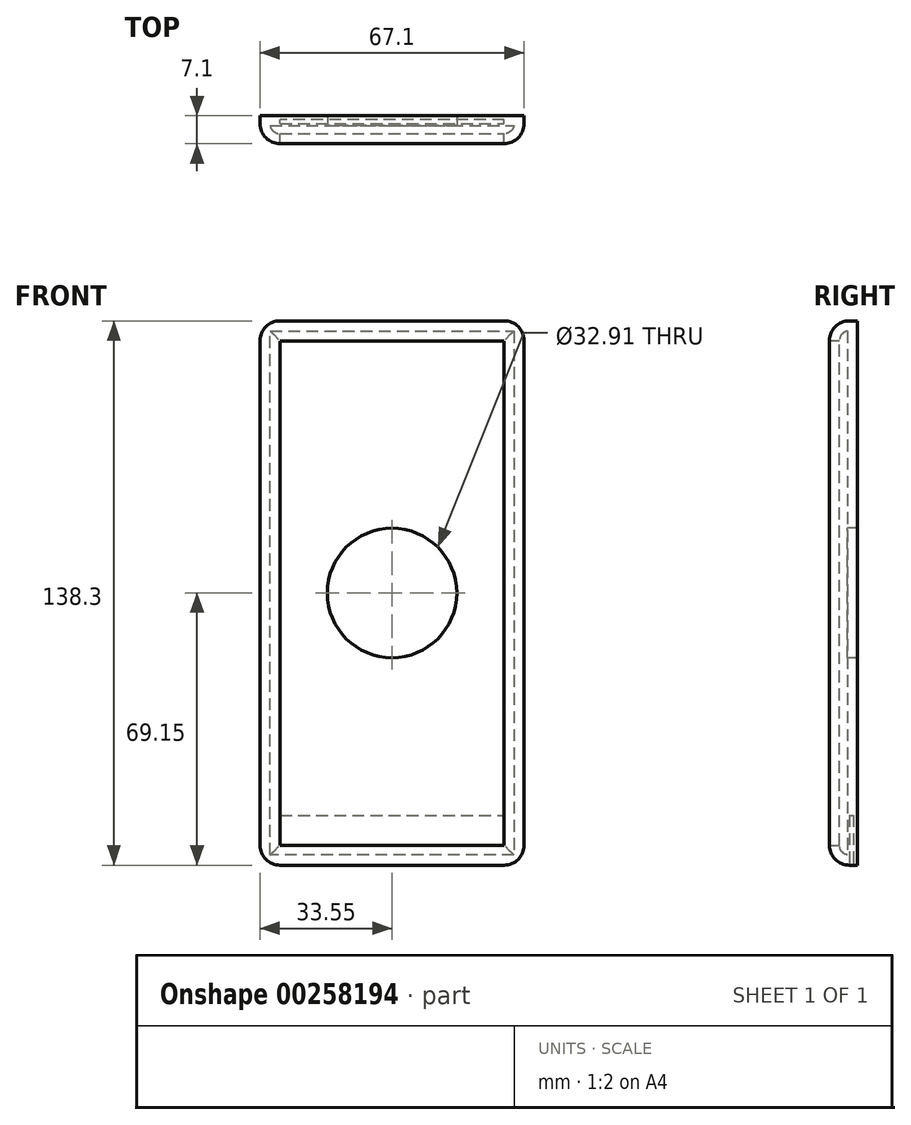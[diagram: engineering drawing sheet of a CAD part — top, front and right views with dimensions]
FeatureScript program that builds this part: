
annotation { "Feature Type Name" : "Feature", "Feature Type Description" : "" }
export const myFeature = defineFeature(function(context is Context, id is Id, definition is map)
    precondition{}
    {
        {
            var Q0;
            Q0=qCreatedBy(makeId("Front.planeOp"),FACE);
            var sketch = newSketch(context, id + "F0", { "sketchPlane" : qUnion([Q0])});
            skLineSegment(sketch, "E0.bottom", {"start": v(-33.55, 69.15) * mm, "end": v(33.55, 69.15) * mm});
            skLineSegment(sketch, "E0.top", {"start": v(-33.55, -69.15) * mm, "end": v(33.55, -69.15) * mm});
            skLineSegment(sketch, "E0.left", {"start": v(-33.55, 69.15) * mm, "end": v(-33.55, -69.15) * mm});
            skLineSegment(sketch, "E0.right", {"start": v(33.55, 69.15) * mm, "end": v(33.55, -69.15) * mm});
            skPoint(sketch, "E0.middle", {"position": v(0, 0) * mm});
            skSolve(sketch);
        }
        {
            var Q0;
            Q0=makeQuery(id+"F0.imprint","IMPRINT",FACE,{"disambiguationData":[TD([[makeQuery(id+"F0.imprint","IMPRINT",EDGE,{"derivedFrom":sQuery(id+"F0.wireOp",EDGE,"E0.bottom")}),-1.0]])]});
            extrude(context, id + "F1", {"entities" : qUnion([Q0]), "depth" : 7.1 * mm});
        }
        {
            var Q0;
            Q0=makeQuery(id+"F1.opExtrude","CAP_EDGE",EDGE,{"disambiguationData":[OSD([sQuery(id+"F0.wireOp",EDGE,"E0.bottom")])],"isStart":false});
            var Q1;
            Q1=makeQuery(id+"F1.opExtrude","CAP_EDGE",EDGE,{"disambiguationData":[OSD([sQuery(id+"F0.wireOp",EDGE,"E0.left")])],"isStart":false});
            var Q2;
            Q2=makeQuery(id+"F1.opExtrude","CAP_FACE",FACE,{"disambiguationData":[OSD([sQuery(id+"F0.wireOp",EDGE,"E0.bottom"),sQuery(id+"F0.wireOp",EDGE,"E0.top"),sQuery(id+"F0.wireOp",EDGE,"E0.left"),sQuery(id+"F0.wireOp",EDGE,"E0.right")])],"isStart":false});
            fillet(context, id + "F2", {"entities" : qUnion([Q0, Q1, Q2]), "radius" : 5.08 * mm, "tangentPropagation" : true, "allowEdgeOverflow" : false});
        }
        {
            var Q0;
            Q0=makeQuery(id+"F1.opExtrude","CAP_FACE",FACE,{"disambiguationData":[OSD([sQuery(id+"F0.wireOp",EDGE,"E0.bottom"),sQuery(id+"F0.wireOp",EDGE,"E0.top"),sQuery(id+"F0.wireOp",EDGE,"E0.left"),sQuery(id+"F0.wireOp",EDGE,"E0.right")])],"isStart":false});
            shell(context, id + "F3", {"entities" : qUnion([Q0]), "thickness" : 2.54 * mm});
        }
        {
            var Q0;
            Q0=makeQuery(id+"F2.opFillet","BLEND_EDGE",EDGE,{"blendedFrom":[makeQuery(id+"F1.opExtrude","CAP_EDGE",EDGE,{"disambiguationData":[OSD([sQuery(id+"F0.wireOp",EDGE,"E0.bottom")])],"isStart":false}),makeQuery(id+"F1.opExtrude","CAP_EDGE",EDGE,{"disambiguationData":[OSD([sQuery(id+"F0.wireOp",EDGE,"E0.left")])],"isStart":false})],"blendedInto":[]});
            var Q1;
            Q1=makeQuery(id+"F2.opFillet","BLEND_EDGE",EDGE,{"blendedFrom":[makeQuery(id+"F1.opExtrude","CAP_EDGE",EDGE,{"disambiguationData":[OSD([sQuery(id+"F0.wireOp",EDGE,"E0.bottom")])],"isStart":false}),makeQuery(id+"F1.opExtrude","CAP_EDGE",EDGE,{"disambiguationData":[OSD([sQuery(id+"F0.wireOp",EDGE,"E0.right")])],"isStart":false})],"blendedInto":[]});
            var Q2;
            Q2=makeQuery(id+"F2.opFillet","BLEND_EDGE",EDGE,{"blendedFrom":[makeQuery(id+"F1.opExtrude","CAP_EDGE",EDGE,{"disambiguationData":[OSD([sQuery(id+"F0.wireOp",EDGE,"E0.top")])],"isStart":false}),makeQuery(id+"F1.opExtrude","CAP_EDGE",EDGE,{"disambiguationData":[OSD([sQuery(id+"F0.wireOp",EDGE,"E0.right")])],"isStart":false})],"blendedInto":[]});
            var Q3;
            Q3=makeQuery(id+"F2.opFillet","BLEND_EDGE",EDGE,{"blendedFrom":[makeQuery(id+"F1.opExtrude","CAP_EDGE",EDGE,{"disambiguationData":[OSD([sQuery(id+"F0.wireOp",EDGE,"E0.top")])],"isStart":false}),makeQuery(id+"F1.opExtrude","CAP_EDGE",EDGE,{"disambiguationData":[OSD([sQuery(id+"F0.wireOp",EDGE,"E0.left")])],"isStart":false})],"blendedInto":[]});
            fillet(context, id + "F4", {"entities" : qUnion([Q0, Q1, Q2, Q3]), "radius" : 5.08 * mm, "tangentPropagation" : true, "allowEdgeOverflow" : false});
        }
        {
            var Q0;
            Q0=makeQuery(id+"F1.opExtrude","SWEPT_FACE",FACE,{"disambiguationData":[OSD([sQuery(id+"F0.wireOp",EDGE,"E0.top")])]});
            var sketch = newSketch(context, id + "F5", { "sketchPlane" : qUnion([Q0])});
            skPoint(sketch, "E1.oppositeSnap0", {"position": v(28.47, 1) * mm});
            skLineSegment(sketch, "E1.bottom", {"start": v(-29.15, 2.02) * mm, "end": v(29.44, 2.02) * mm});
            skLineSegment(sketch, "E1.top", {"start": v(-29.15, 1) * mm, "end": v(29.44, 1) * mm});
            skLineSegment(sketch, "E1.left", {"start": v(-29.15, 2.02) * mm, "end": v(-29.15, 1) * mm});
            skLineSegment(sketch, "E1.right", {"start": v(29.44, 2.02) * mm, "end": v(29.44, 1) * mm});
            skSolve(sketch);
        }
        {
            var Q0;
            Q0=makeQuery(id+"F5.imprint","IMPRINT",FACE,{"disambiguationData":[TD([[makeQuery(id+"F5.imprint","IMPRINT",EDGE,{"derivedFrom":sQuery(id+"F5.wireOp",EDGE,"E1.bottom")}),1.0]])]});
            extrude(context, id + "F6", {"entities" : qUnion([Q0]), "operationType" : NewBodyOperationType.REMOVE, "endBound" : BoundingType.SYMMETRIC, "oppositeDirection" : true, "depth" : 25.4 * mm});
        }
        {
            var Q0;
            Q0=makeQuery(id+"F3.opShell","OFFSET_FACE",FACE,{"disambiguationData":[OSD([sQuery(id+"F0.wireOp",EDGE,"E0.bottom"),sQuery(id+"F0.wireOp",EDGE,"E0.top"),sQuery(id+"F0.wireOp",EDGE,"E0.left"),sQuery(id+"F0.wireOp",EDGE,"E0.right")])]});
            var sketch = newSketch(context, id + "F7", { "sketchPlane" : qUnion([Q0])});
            skCircle(sketch, "E2", {"center": v(0, 0) * mm, "radius": 16.45 * mm});
            skSolve(sketch);
        }
        {
            var Q0;
            Q0=makeQuery(id+"F7.imprint","IMPRINT",FACE,{"disambiguationData":[TD([[makeQuery(id+"F7.imprint","IMPRINT",EDGE,{"derivedFrom":sQuery(id+"F7.wireOp",EDGE,"E2")}),1.0]])]});
            extrude(context, id + "F8", {"entities" : qUnion([Q0]), "operationType" : NewBodyOperationType.REMOVE, "endBound" : BoundingType.SYMMETRIC, "oppositeDirection" : true, "depth" : 25.4 * mm});
        }
        {
            var Q0;
            Q0=makeQuery(id+"F3.opShell","OFFSET_FACE",FACE,{"disambiguationData":[OSD([sQuery(id+"F0.wireOp",EDGE,"E0.bottom"),sQuery(id+"F0.wireOp",EDGE,"E0.top"),sQuery(id+"F0.wireOp",EDGE,"E0.left"),sQuery(id+"F0.wireOp",EDGE,"E0.right")])]});
            var sketch = newSketch(context, id + "F9", { "sketchPlane" : qUnion([Q0])});
            skLineSegment(sketch, "E3.bottom", {"start": v(8.16, 53.78) * mm, "end": v(23.6, 53.78) * mm});
            skLineSegment(sketch, "E3.top", {"start": v(8.16, 61.65) * mm, "end": v(23.6, 61.65) * mm});
            skLineSegment(sketch, "E3.left", {"start": v(8.16, 53.78) * mm, "end": v(8.16, 61.65) * mm});
            skLineSegment(sketch, "E3.right", {"start": v(23.6, 53.78) * mm, "end": v(23.6, 61.65) * mm});
            skSolve(sketch);
        }
        {
            var Q0;
            Q0=makeQuery(id+"F9.imprint","IMPRINT",FACE,{"disambiguationData":[TD([[makeQuery(id+"F9.imprint","IMPRINT",EDGE,{"derivedFrom":sQuery(id+"F9.wireOp",EDGE,"E3.bottom")}),1.0]])]});
            extrude(context, id + "F10", {"entities" : qUnion([Q0]), "operationType" : NewBodyOperationType.REMOVE, "endBound" : BoundingType.SYMMETRIC, "oppositeDirection" : true, "depth" : 25.4 * mm});
        }
    });
